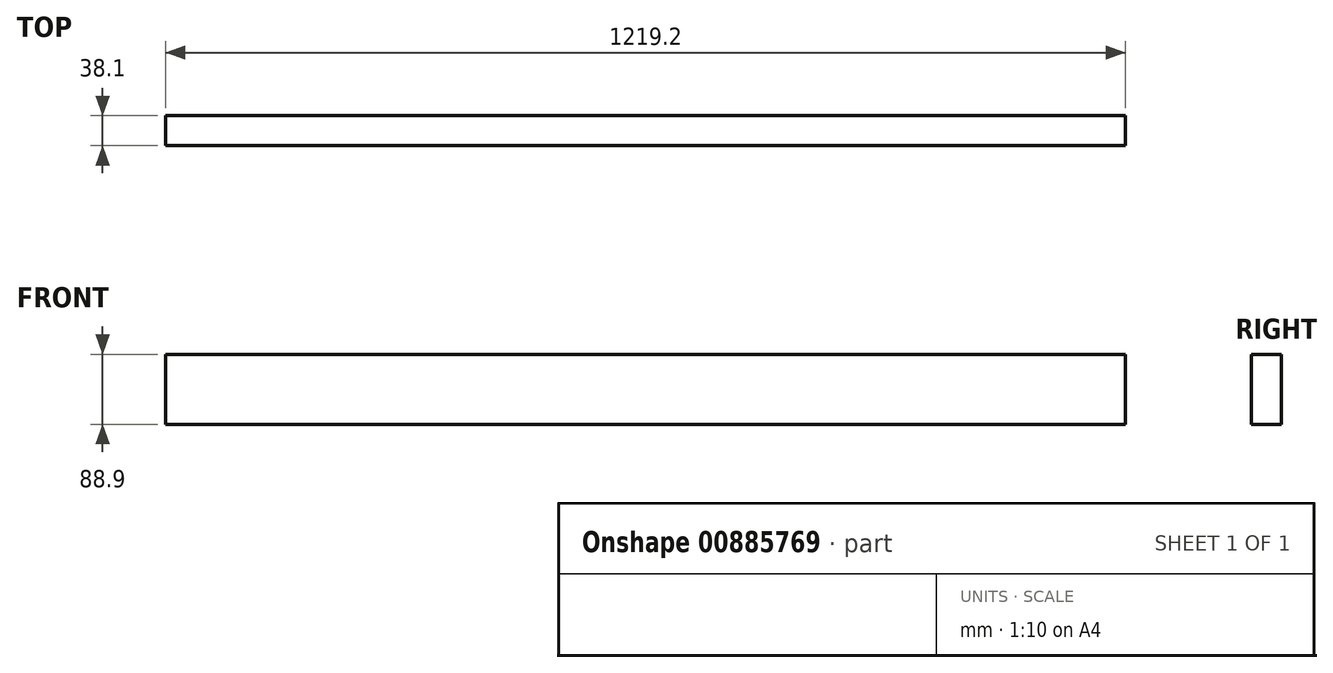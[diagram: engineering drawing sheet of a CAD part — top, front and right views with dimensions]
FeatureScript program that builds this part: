
annotation { "Feature Type Name" : "Feature", "Feature Type Description" : "" }
export const myFeature = defineFeature(function(context is Context, id is Id, definition is map)
    precondition{}
    {
        {
            var Q0;
            Q0=qCreatedBy(makeId("Right.planeOp"),FACE);
            var sketch = newSketch(context, id + "F0", { "sketchPlane" : qUnion([Q0])});
            skLineSegment(sketch, "E0.bottom", {"start": v(19.05, -44.45) * mm, "end": v(-19.05, -44.45) * mm});
            skLineSegment(sketch, "E0.top", {"start": v(19.05, 44.45) * mm, "end": v(-19.05, 44.45) * mm});
            skLineSegment(sketch, "E0.left", {"start": v(19.05, -44.45) * mm, "end": v(19.05, 44.45) * mm});
            skLineSegment(sketch, "E0.right", {"start": v(-19.05, -44.45) * mm, "end": v(-19.05, 44.45) * mm});
            skPoint(sketch, "E0.middle", {"position": v(0, 0) * mm});
            skSolve(sketch);
        }
        {
            var Q0;
            Q0=makeQuery(id+"F0.imprint","IMPRINT",FACE,{"disambiguationData":[TD([[makeQuery(id+"F0.imprint","IMPRINT",EDGE,{"derivedFrom":sQuery(id+"F0.wireOp",EDGE,"E0.bottom")}),-1.0]])]});
            extrude(context, id + "F1", {"entities" : qUnion([Q0]), "endBound" : BoundingType.SYMMETRIC, "depth" : 1219.2 * mm, "offsetDistance" : 25.4 * mm});
        }
    });
